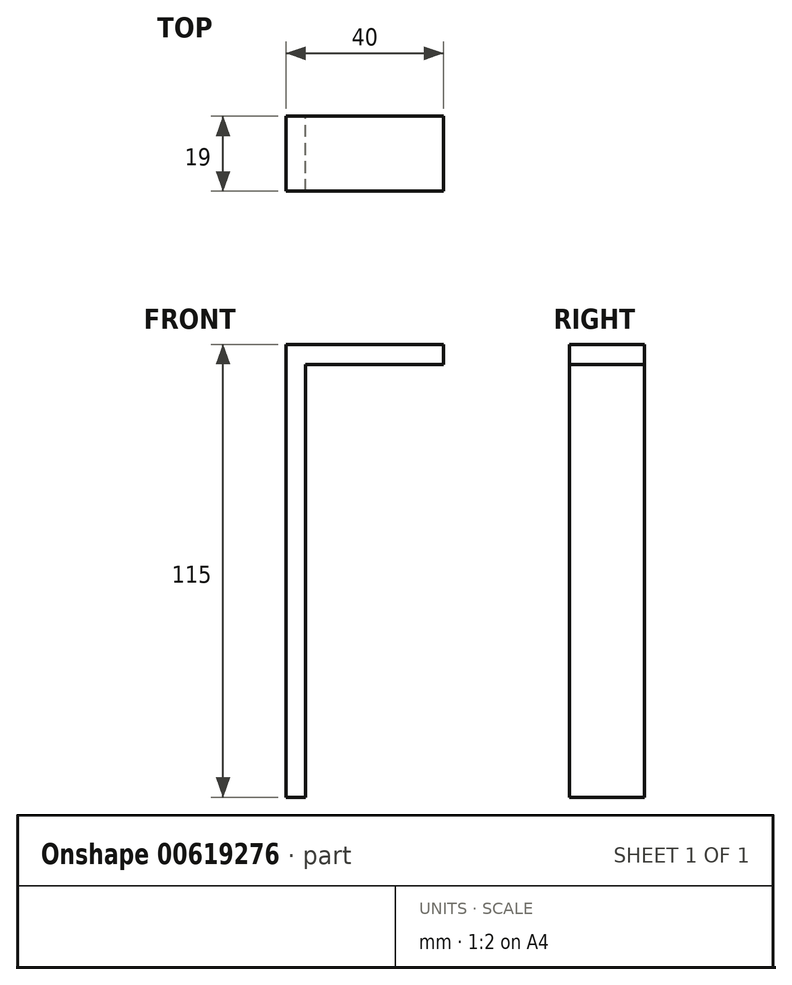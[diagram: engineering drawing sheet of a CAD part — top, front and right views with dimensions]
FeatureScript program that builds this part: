
annotation { "Feature Type Name" : "Feature", "Feature Type Description" : "" }
export const myFeature = defineFeature(function(context is Context, id is Id, definition is map)
    precondition{}
    {
        {
            var Q0;
            Q0=qCreatedBy(makeId("Front.planeOp"),FACE);
            var sketch = newSketch(context, id + "F0", { "sketchPlane" : qUnion([Q0])});
            skLineSegment(sketch, "E0.bottom", {"start": v(-36.5, 45.36) * mm, "end": v(-31.5, 45.36) * mm});
            skLineSegment(sketch, "E0.top", {"start": v(-36.5, -69.64) * mm, "end": v(-31.5, -69.64) * mm});
            skLineSegment(sketch, "E0.left", {"start": v(-36.5, 45.36) * mm, "end": v(-36.5, -69.64) * mm});
            skLineSegment(sketch, "E0.right", {"start": v(-31.5, 40.36) * mm, "end": v(-31.5, -69.64) * mm});
            skLineSegment(sketch, "E1.bottom", {"start": v(-31.5, 45.36) * mm, "end": v(3.5, 45.36) * mm});
            skLineSegment(sketch, "E1.top", {"start": v(-31.5, 40.36) * mm, "end": v(3.5, 40.36) * mm});
            skLineSegment(sketch, "E1.right", {"start": v(3.5, 45.36) * mm, "end": v(3.5, 40.36) * mm});
            skSolve(sketch);
        }
        {
            var Q0;
            Q0 = qSketchRegion(id + "F0", true);
            extrude(context, id + "F1", {"entities" : qUnion([Q0]), "depth" : 19 * mm, "offsetDistance" : 25.4 * mm});
        }
    });
